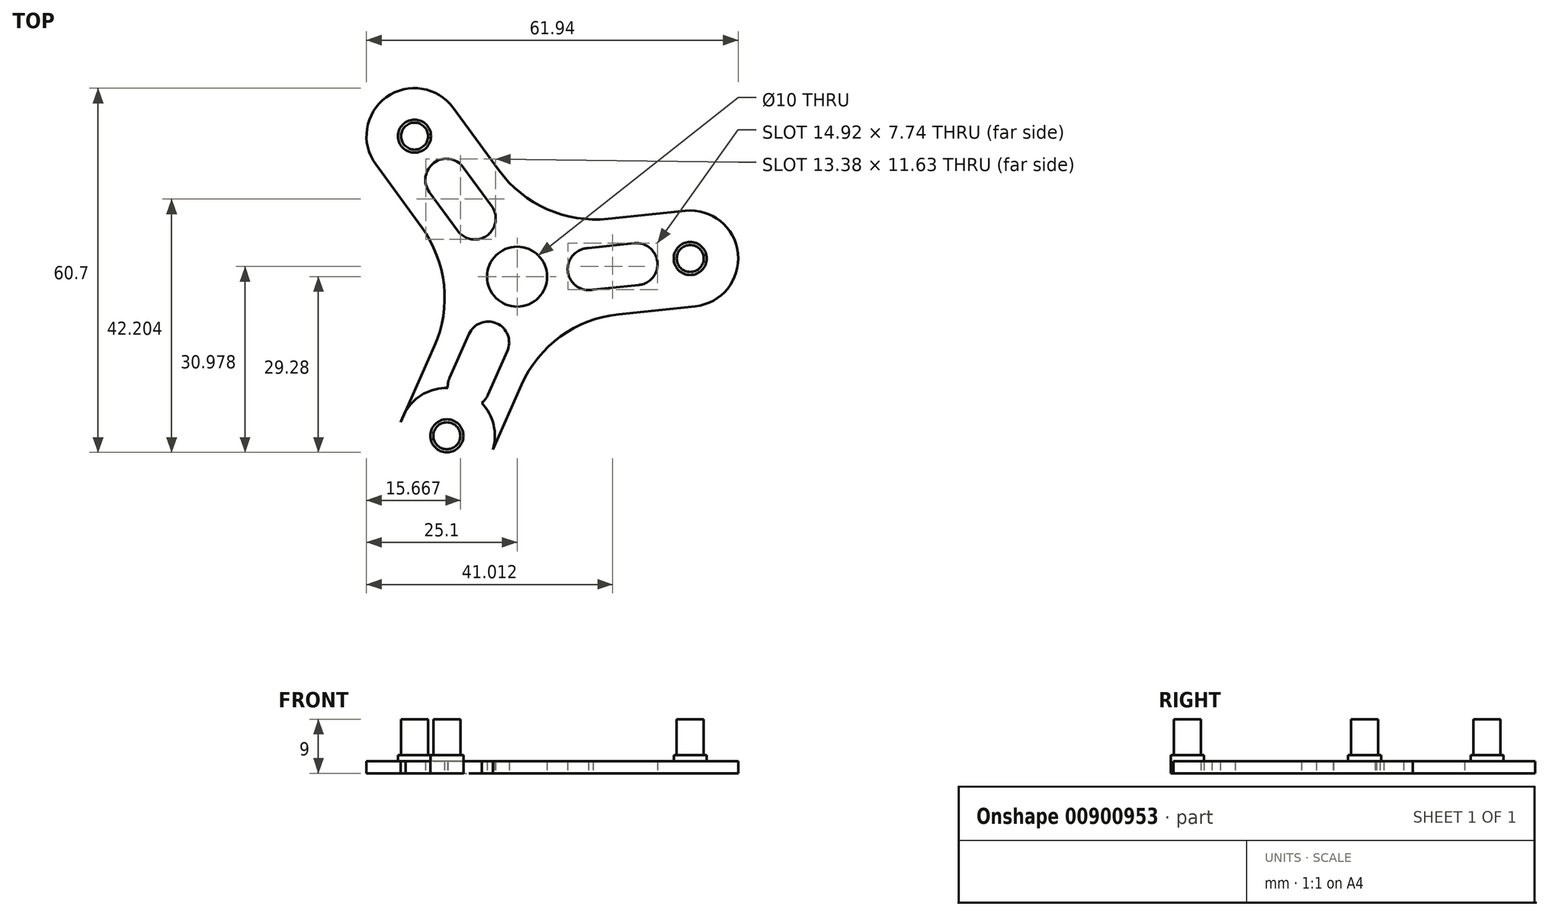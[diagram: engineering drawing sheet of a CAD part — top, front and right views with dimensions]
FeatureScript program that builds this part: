
annotation { "Feature Type Name" : "Feature", "Feature Type Description" : "" }
export const myFeature = defineFeature(function(context is Context, id is Id, definition is map)
    precondition{}
    {
        {
            var Q0;
            Q0=qCreatedBy(makeId("Top.planeOp"),FACE);
            var sketch = newSketch(context, id + "F0", { "sketchPlane" : qUnion([Q0])});
            skCircle(sketch, "E0", {"center": v(0, 0) * mm, "radius": 5 * mm});
            skCircle(sketch, "E1.cCircle", {"center": v(0.02, -0.03) * mm, "radius": 6.16 * mm, "construction": true});
            skLineSegment(sketch, "E1.0", {"start": v(-7.25, 9.93) * mm, "end": v(12.28, 1.29) * mm, "construction": true});
            skLineSegment(sketch, "E1.1", {"start": v(12.28, 1.29) * mm, "end": v(-4.97, -11.3) * mm, "construction": true});
            skLineSegment(sketch, "E1.2", {"start": v(-4.97, -11.3) * mm, "end": v(-7.25, 9.93) * mm, "construction": true});
            skPoint(sketch, "E1.0.midPoint", {"position": v(2.51, 5.61) * mm});
            skLineSegment(sketch, "E2", {"start": v(0, 0) * mm, "end": v(41.18, 4.33) * mm, "construction": true});
            skLineSegment(sketch, "E3", {"start": v(-12.12, -27.46) * mm, "end": v(0.02, -0.03) * mm, "construction": true});
            skLineSegment(sketch, "E4", {"start": v(0, 0) * mm, "end": v(-17.77, 24.35) * mm, "construction": true});
            skCircle(sketch, "E5", {"center": v(28.84, 3.03) * mm, "radius": 8 * mm});
            skCircle(sketch, "E6", {"center": v(-17.1, 23.42) * mm, "radius": 8 * mm});
            skCircle(sketch, "E7", {"center": v(-11.71, -26.53) * mm, "radius": 8 * mm});
            skLineSegment(sketch, "E8", {"start": v(-23.56, 18.7) * mm, "end": v(-10.64, 28.14) * mm, "construction": true});
            skLineSegment(sketch, "E9", {"start": v(28, 10.99) * mm, "end": v(29.68, -4.93) * mm, "construction": true});
            skLineSegment(sketch, "E10", {"start": v(-19.38, -24.25) * mm, "end": v(-4.87, -30.67) * mm, "construction": true});
            skLineSegment(sketch, "E11", {"start": v(-19.38, -24.25) * mm, "end": v(-9.12, -1.07) * mm});
            skLineSegment(sketch, "E12", {"start": v(-23.56, 18.7) * mm, "end": v(-9.12, -1.07) * mm});
            skLineSegment(sketch, "E13", {"start": v(-10.64, 28.14) * mm, "end": v(3.75, 8.44) * mm});
            skLineSegment(sketch, "E14", {"start": v(28, 10.99) * mm, "end": v(3.75, 8.44) * mm});
            skLineSegment(sketch, "E15", {"start": v(29.68, -4.93) * mm, "end": v(5.4, -7.48) * mm});
            skLineSegment(sketch, "E16", {"start": v(-4.87, -30.67) * mm, "end": v(5.4, -7.48) * mm});
            skCircle(sketch, "E17", {"center": v(-17.1, 23.42) * mm, "radius": 2.25 * mm});
            skCircle(sketch, "E18", {"center": v(-17.1, 23.42) * mm, "radius": 2.75 * mm});
            skCircle(sketch, "E19", {"center": v(28.84, 3.03) * mm, "radius": 2.25 * mm});
            skCircle(sketch, "E20", {"center": v(28.84, 3.03) * mm, "radius": 2.75 * mm});
            skCircle(sketch, "E21", {"center": v(-11.71, -26.53) * mm, "radius": 2.25 * mm});
            skCircle(sketch, "E22", {"center": v(-11.71, -26.53) * mm, "radius": 2.75 * mm});
            skCircle(sketch, "E23", {"center": v(-11.8, 16.15) * mm, "radius": 3.5 * mm});
            skCircle(sketch, "E24", {"center": v(-7.07, 9.7) * mm, "radius": 3.5 * mm});
            skCircle(sketch, "E25", {"center": v(11.93, 1.25) * mm, "radius": 3.5 * mm});
            skCircle(sketch, "E26", {"center": v(19.9, 2.09) * mm, "radius": 3.5 * mm});
            skCircle(sketch, "E27", {"center": v(-8.07, -18.3) * mm, "radius": 3.5 * mm});
            skCircle(sketch, "E28", {"center": v(-4.83, -10.98) * mm, "radius": 3.5 * mm});
            skLineSegment(sketch, "E29", {"start": v(11.91, 4.75) * mm, "end": v(12.64, -2.17) * mm, "construction": true});
            skLineSegment(sketch, "E30", {"start": v(19.52, 5.57) * mm, "end": v(20.26, -1.4) * mm, "construction": true});
            skLineSegment(sketch, "E31", {"start": v(19.52, 5.57) * mm, "end": v(11.91, 4.75) * mm});
            skLineSegment(sketch, "E32", {"start": v(12.64, -2.17) * mm, "end": v(20.26, -1.4) * mm});
            skLineSegment(sketch, "E33", {"start": v(-8.03, -9.57) * mm, "end": v(-1.63, -12.4) * mm, "construction": true});
            skLineSegment(sketch, "E34", {"start": v(-11.27, -16.88) * mm, "end": v(-4.87, -19.72) * mm, "construction": true});
            skLineSegment(sketch, "E35", {"start": v(-11.27, -16.88) * mm, "end": v(-8.03, -9.57) * mm});
            skLineSegment(sketch, "E36", {"start": v(-1.63, -12.4) * mm, "end": v(-4.87, -19.72) * mm});
            skLineSegment(sketch, "E37", {"start": v(-14.62, 14.1) * mm, "end": v(-8.96, 18.22) * mm, "construction": true});
            skLineSegment(sketch, "E38", {"start": v(-9.9, 7.63) * mm, "end": v(-4.25, 11.76) * mm, "construction": true});
            skLineSegment(sketch, "E39", {"start": v(-8.96, 18.22) * mm, "end": v(-4.25, 11.76) * mm});
            skLineSegment(sketch, "E40", {"start": v(-9.9, 7.63) * mm, "end": v(-14.62, 14.1) * mm});
            skSolve(sketch);
        }
        {
            var Q0;
            {var subQ0=sQuery(id+"F0.wireOp",EDGE,"E6");var subQ1=makeQuery(id+"F0.imprint","INTERSECT",VERTEX,{"derivedFrom":[subQ0,sQuery(id+"F0.wireOp",EDGE,"E12")]});Q0=makeQuery(id+"F0.imprint","IMPRINT",FACE,{"disambiguationData":[TD([[makeQuery(id+"F0.imprint","IMPRINT",EDGE,{"disambiguationData":[TD([[subQ1,1.0]])],"derivedFrom":subQ0}),1.0]])]});}
            var Q1;
            {var subQ0=sQuery(id+"F0.wireOp",EDGE,"E11");var subQ1=sQuery(id+"F0.wireOp",EDGE,"E7");var subQ2=makeQuery(id+"F0.imprint","INTERSECT",VERTEX,{"disambiguationData":[OD(0.0)],"derivedFrom":[subQ1,subQ0]});Q1=makeQuery(id+"F0.imprint","IMPRINT",FACE,{"disambiguationData":[TD([[makeQuery(id+"F0.imprint","IMPRINT",EDGE,{"disambiguationData":[TD([[subQ2,-1.0]])],"derivedFrom":subQ1}),1.0]])]});}
            var Q2;
            {var subQ0=sQuery(id+"F0.wireOp",EDGE,"E5");var subQ1=makeQuery(id+"F0.imprint","INTERSECT",VERTEX,{"derivedFrom":[subQ0,sQuery(id+"F0.wireOp",EDGE,"E14")]});Q2=makeQuery(id+"F0.imprint","IMPRINT",FACE,{"disambiguationData":[TD([[makeQuery(id+"F0.imprint","IMPRINT",EDGE,{"disambiguationData":[TD([[subQ1,-1.0]])],"derivedFrom":subQ0}),1.0]])]});}
            var Q3;
            Q3=makeQuery(id+"F0.imprint","IMPRINT",FACE,{"disambiguationData":[TD([[makeQuery(id+"F0.imprint","IMPRINT",EDGE,{"derivedFrom":sQuery(id+"F0.wireOp",EDGE,"E0")}),-1.0]])]});
            var Q4;
            Q4=makeQuery(id+"F0.imprint","IMPRINT",FACE,{"disambiguationData":[TD([[makeQuery(id+"F0.imprint","IMPRINT",EDGE,{"derivedFrom":sQuery(id+"F0.wireOp",EDGE,"E17")}),-1.0]])]});
            var Q5;
            Q5=makeQuery(id+"F0.imprint","IMPRINT",FACE,{"disambiguationData":[TD([[makeQuery(id+"F0.imprint","IMPRINT",EDGE,{"derivedFrom":sQuery(id+"F0.wireOp",EDGE,"E17")}),1.0]])]});
            var Q6;
            Q6=makeQuery(id+"F0.imprint","IMPRINT",FACE,{"disambiguationData":[TD([[makeQuery(id+"F0.imprint","IMPRINT",EDGE,{"derivedFrom":sQuery(id+"F0.wireOp",EDGE,"E21")}),1.0]])]});
            var Q7;
            Q7=makeQuery(id+"F0.imprint","IMPRINT",FACE,{"disambiguationData":[TD([[makeQuery(id+"F0.imprint","IMPRINT",EDGE,{"derivedFrom":sQuery(id+"F0.wireOp",EDGE,"E21")}),-1.0]])]});
            var Q8;
            Q8=makeQuery(id+"F0.imprint","IMPRINT",FACE,{"disambiguationData":[TD([[makeQuery(id+"F0.imprint","IMPRINT",EDGE,{"derivedFrom":sQuery(id+"F0.wireOp",EDGE,"E19")}),1.0]])]});
            var Q9;
            Q9=makeQuery(id+"F0.imprint","IMPRINT",FACE,{"disambiguationData":[TD([[makeQuery(id+"F0.imprint","IMPRINT",EDGE,{"derivedFrom":sQuery(id+"F0.wireOp",EDGE,"E19")}),-1.0]])]});
            extrude(context, id + "F1", {"entities" : qUnion([Q0, Q1, Q2, Q3, Q4, Q5, Q6, Q7, Q8, Q9]), "depth" : 2 * mm, "offsetDistance" : 25 * mm});
        }
        {
            var Q0;
            Q0=makeQuery(id+"F0.imprint","IMPRINT",FACE,{"disambiguationData":[TD([[makeQuery(id+"F0.imprint","IMPRINT",EDGE,{"derivedFrom":sQuery(id+"F0.wireOp",EDGE,"E17")}),-1.0]])]});
            var Q1;
            Q1=makeQuery(id+"F0.imprint","IMPRINT",FACE,{"disambiguationData":[TD([[makeQuery(id+"F0.imprint","IMPRINT",EDGE,{"derivedFrom":sQuery(id+"F0.wireOp",EDGE,"E17")}),1.0]])]});
            var Q2;
            Q2=makeQuery(id+"F0.imprint","IMPRINT",FACE,{"disambiguationData":[TD([[makeQuery(id+"F0.imprint","IMPRINT",EDGE,{"derivedFrom":sQuery(id+"F0.wireOp",EDGE,"E19")}),1.0]])]});
            var Q3;
            Q3=makeQuery(id+"F0.imprint","IMPRINT",FACE,{"disambiguationData":[TD([[makeQuery(id+"F0.imprint","IMPRINT",EDGE,{"derivedFrom":sQuery(id+"F0.wireOp",EDGE,"E19")}),-1.0]])]});
            var Q4;
            Q4=makeQuery(id+"F0.imprint","IMPRINT",FACE,{"disambiguationData":[TD([[makeQuery(id+"F0.imprint","IMPRINT",EDGE,{"derivedFrom":sQuery(id+"F0.wireOp",EDGE,"E21")}),1.0]])]});
            var Q5;
            Q5=makeQuery(id+"F0.imprint","IMPRINT",FACE,{"disambiguationData":[TD([[makeQuery(id+"F0.imprint","IMPRINT",EDGE,{"derivedFrom":sQuery(id+"F0.wireOp",EDGE,"E21")}),-1.0]])]});
            extrude(context, id + "F2", {"entities" : qUnion([Q0, Q1, Q2, Q3, Q4, Q5]), "operationType" : NewBodyOperationType.ADD, "depth" : 3 * mm, "offsetDistance" : 25 * mm});
        }
        {
            var Q0;
            Q0=makeQuery(id+"F0.imprint","IMPRINT",FACE,{"disambiguationData":[TD([[makeQuery(id+"F0.imprint","IMPRINT",EDGE,{"derivedFrom":sQuery(id+"F0.wireOp",EDGE,"E21")}),1.0]])]});
            var Q1;
            Q1=makeQuery(id+"F0.imprint","IMPRINT",FACE,{"disambiguationData":[TD([[makeQuery(id+"F0.imprint","IMPRINT",EDGE,{"derivedFrom":sQuery(id+"F0.wireOp",EDGE,"E17")}),1.0]])]});
            var Q2;
            Q2=makeQuery(id+"F0.imprint","IMPRINT",FACE,{"disambiguationData":[TD([[makeQuery(id+"F0.imprint","IMPRINT",EDGE,{"derivedFrom":sQuery(id+"F0.wireOp",EDGE,"E19")}),1.0]])]});
            extrude(context, id + "F3", {"entities" : qUnion([Q0, Q1, Q2]), "operationType" : NewBodyOperationType.ADD, "depth" : 9 * mm, "offsetDistance" : 25 * mm});
        }
        {
            var Q0;
            Q0=makeQuery(id+"F1.opExtrude","SWEPT_EDGE",EDGE,{"disambiguationData":[OSD([sQuery(id+"F0.wireOp",EDGE,"E13"),sQuery(id+"F0.wireOp",EDGE,"E14")])]});
            fillet(context, id + "F4", {"entities" : qUnion([Q0]), "radius" : 20 * mm, "tangentPropagation" : true, "allowEdgeOverflow" : false});
        }
        {
            var Q0;
            Q0=makeQuery(id+"F1.opExtrude","SWEPT_EDGE",EDGE,{"disambiguationData":[OSD([sQuery(id+"F0.wireOp",EDGE,"E11"),sQuery(id+"F0.wireOp",EDGE,"E12")])]});
            fillet(context, id + "F5", {"entities" : qUnion([Q0]), "radius" : 20 * mm, "tangentPropagation" : true, "allowEdgeOverflow" : false});
        }
        {
            var Q0;
            Q0=makeQuery(id+"F1.opExtrude","SWEPT_EDGE",EDGE,{"disambiguationData":[OSD([sQuery(id+"F0.wireOp",EDGE,"E15"),sQuery(id+"F0.wireOp",EDGE,"E16")])]});
            fillet(context, id + "F6", {"entities" : qUnion([Q0]), "radius" : 20 * mm, "tangentPropagation" : true, "allowEdgeOverflow" : false});
        }
    });
